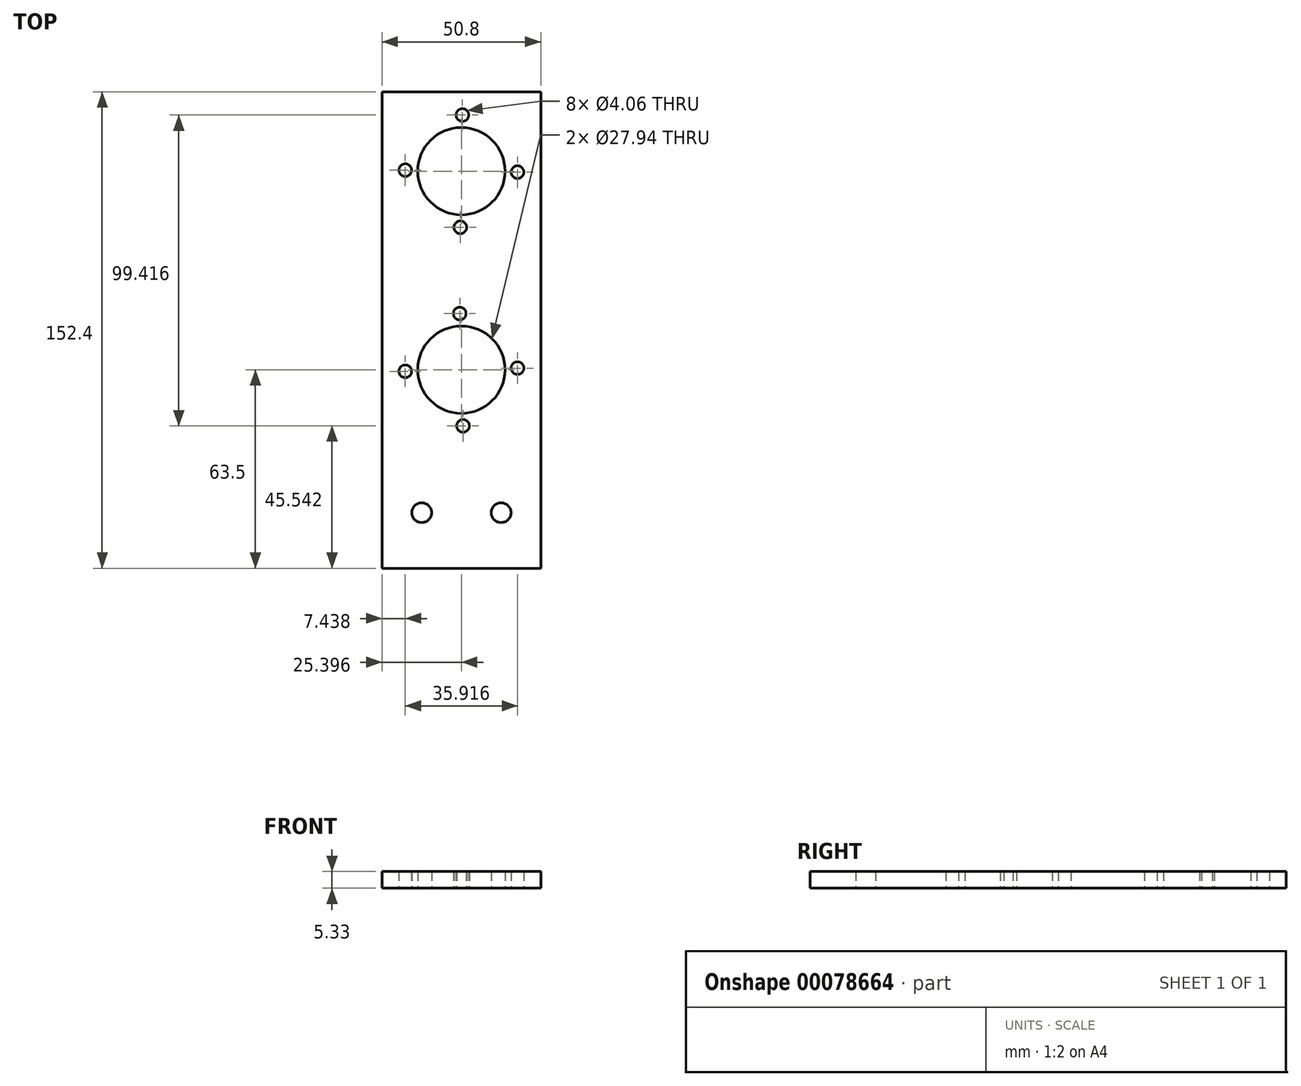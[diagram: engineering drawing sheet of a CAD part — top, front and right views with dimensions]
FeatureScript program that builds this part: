
annotation { "Feature Type Name" : "Feature", "Feature Type Description" : "" }
export const myFeature = defineFeature(function(context is Context, id is Id, definition is map)
    precondition{}
    {
        {
            var Q0;
            Q0=qCreatedBy(makeId("Top.planeOp"),FACE);
            var sketch = newSketch(context, id + "F0", { "sketchPlane" : qUnion([Q0])});
            skCircle(sketch, "E0", {"center": v(-17.73, 78.74) * mm, "radius": 2.03 * mm});
            skCircle(sketch, "E1.1.0", {"center": v(-36.01, 61.1) * mm, "radius": 2.03 * mm});
            skCircle(sketch, "E1.2.0", {"center": v(-18.38, 42.82) * mm, "radius": 2.03 * mm});
            skCircle(sketch, "E1.3.0", {"center": v(-0.1, 60.46) * mm, "radius": 2.03 * mm});
            skPoint(sketch, "E1.center", {"position": v(-18.05, 60.78) * mm});
            skCircle(sketch, "E2", {"center": v(-18.05, 60.78) * mm, "radius": 13.97 * mm});
            skLineSegment(sketch, "E3.top", {"start": v(7.35, 86.18) * mm, "end": v(-43.45, 86.18) * mm});
            skLineSegment(sketch, "E4.top", {"start": v(7.35, -66.22) * mm, "end": v(-43.45, -66.22) * mm});
            skLineSegment(sketch, "E5", {"start": v(7.35, 86.18) * mm, "end": v(7.35, -66.22) * mm});
            skLineSegment(sketch, "E6", {"start": v(-43.45, -66.22) * mm, "end": v(-43.45, 86.18) * mm});
            skCircle(sketch, "E7", {"center": v(-18.57, 15.24) * mm, "radius": 2.03 * mm});
            skCircle(sketch, "E8.1.0", {"center": v(-36.01, -3.24) * mm, "radius": 2.03 * mm});
            skCircle(sketch, "E8.2.0", {"center": v(-17.53, -20.68) * mm, "radius": 2.03 * mm});
            skCircle(sketch, "E8.3.0", {"center": v(-0.1, -2.2) * mm, "radius": 2.03 * mm});
            skPoint(sketch, "E8.center", {"position": v(-18.05, -2.72) * mm});
            skCircle(sketch, "E9", {"center": v(-18.05, -2.72) * mm, "radius": 13.97 * mm});
            skSolve(sketch);
        }
        {
            var Q0;
            Q0=qSketchRegion(id+"F0",true);
            extrude(context, id + "F1", {"entities" : qUnion([Q0]), "depth" : 5.33 * mm});
        }
        {
            var Q0;
            Q0=makeQuery(id+"F1.opExtrude","CAP_FACE",FACE,{"disambiguationData":[OSD([sQuery(id+"F0.wireOp",EDGE,"E0"),sQuery(id+"F0.wireOp",EDGE,"E1.1.0"),sQuery(id+"F0.wireOp",EDGE,"E1.2.0"),sQuery(id+"F0.wireOp",EDGE,"E1.3.0"),sQuery(id+"F0.wireOp",EDGE,"E2"),sQuery(id+"F0.wireOp",EDGE,"E3.top"),sQuery(id+"F0.wireOp",EDGE,"E4.top"),sQuery(id+"F0.wireOp",EDGE,"E5"),sQuery(id+"F0.wireOp",EDGE,"E6")])],"isStart":true});
            var sketch = newSketch(context, id + "F2", { "sketchPlane" : qUnion([Q0])});
            skCircle(sketch, "E10", {"center": v(-5.35, 48.44) * mm, "radius": 3.18 * mm});
            skCircle(sketch, "E11", {"center": v(-30.75, 48.44) * mm, "radius": 3.18 * mm});
            skSolve(sketch);
        }
        {
            var Q0;
            Q0=qSketchRegion(id+"F2",true);
            extrude(context, id + "F3", {"entities" : qUnion([Q0]), "operationType" : NewBodyOperationType.REMOVE, "oppositeDirection" : true, "depth" : 25.4 * mm});
        }
    });
